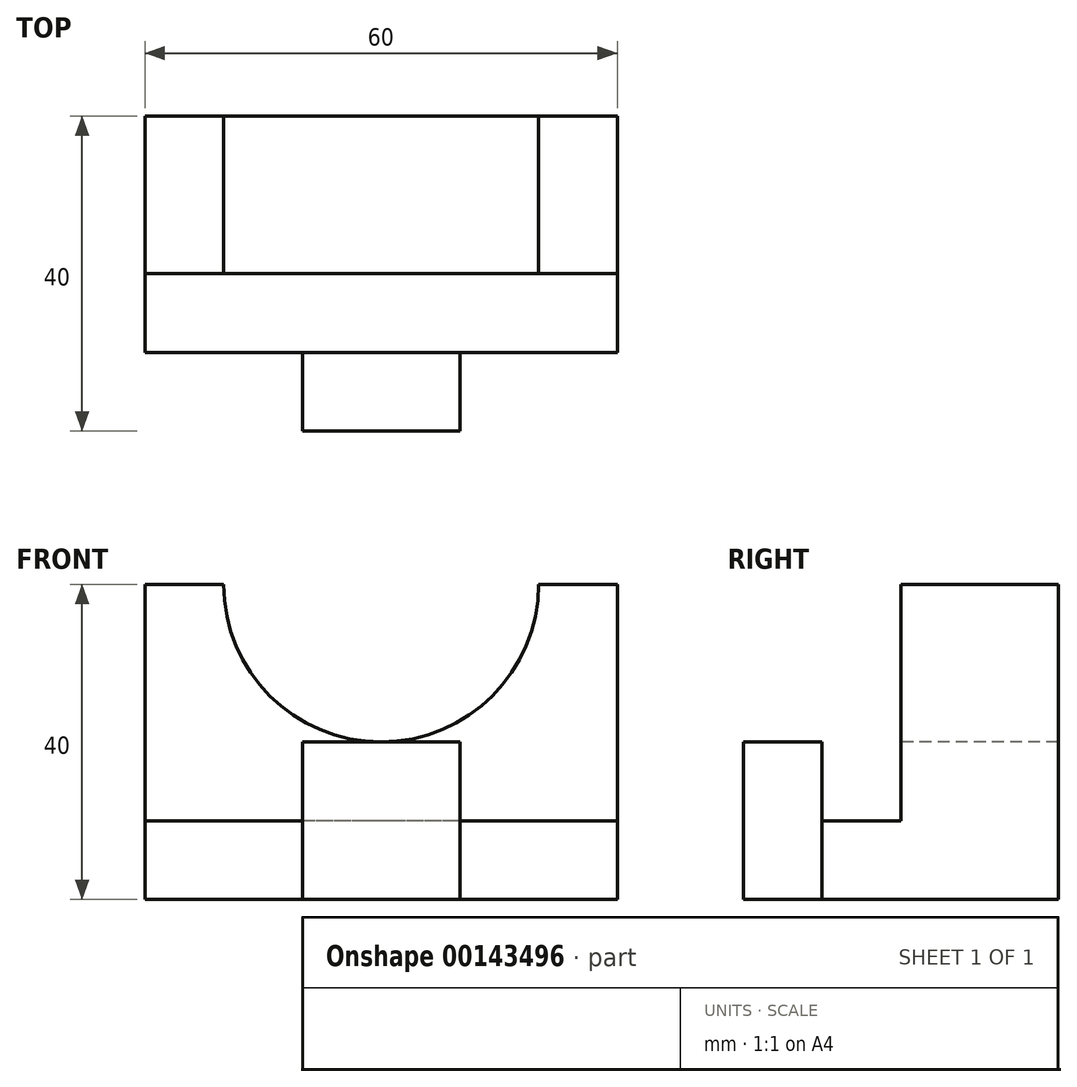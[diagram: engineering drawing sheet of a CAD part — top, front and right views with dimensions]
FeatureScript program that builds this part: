
annotation { "Feature Type Name" : "Feature", "Feature Type Description" : "" }
export const myFeature = defineFeature(function(context is Context, id is Id, definition is map)
    precondition{}
    {
        {
            var Q0;
            Q0=qCreatedBy(makeId("Right.planeOp"),FACE);
            var sketch = newSketch(context, id + "F0", { "sketchPlane" : qUnion([Q0])});
            skLineSegment(sketch, "E0", {"start": v(0, 0) * mm, "end": v(0, 40) * mm});
            skLineSegment(sketch, "E1", {"start": v(0, 40) * mm, "end": v(-20, 40) * mm});
            skLineSegment(sketch, "E2", {"start": v(-20, 40) * mm, "end": v(-20, 10) * mm});
            skLineSegment(sketch, "E3", {"start": v(-20, 10) * mm, "end": v(-30, 10) * mm});
            skLineSegment(sketch, "E4", {"start": v(-30, 10) * mm, "end": v(-30, 0) * mm});
            skLineSegment(sketch, "E5", {"start": v(-30, 0) * mm, "end": v(0, 0) * mm});
            skSolve(sketch);
        }
        {
            var Q0;
            Q0=makeQuery(id+"F0.imprint","IMPRINT",FACE,{"disambiguationData":[TD([[makeQuery(id+"F0.imprint","IMPRINT",EDGE,{"derivedFrom":sQuery(id+"F0.wireOp",EDGE,"E0")}),1.0]])]});
            extrude(context, id + "F1", {"entities" : qUnion([Q0]), "endBound" : BoundingType.SYMMETRIC, "depth" : 60 * mm});
        }
        {
            var Q0;
            Q0=makeQuery(id+"F1.opExtrude","SWEPT_FACE",FACE,{"disambiguationData":[OSD([sQuery(id+"F0.wireOp",EDGE,"E2")])]});
            var sketch = newSketch(context, id + "F2", { "sketchPlane" : qUnion([Q0])});
            skArc(sketch, "E6", {"start": v(-20, 40) * mm, "mid": v(0, 20) * mm, "end": v(20, 40) * mm});
            skLineSegment(sketch, "E7", {"start": v(-20, 40) * mm, "end": v(20, 40) * mm});
            skSolve(sketch);
        }
        {
            var Q0;
            Q0=makeQuery(id+"F2.imprint","IMPRINT",FACE,{"disambiguationData":[TD([[makeQuery(id+"F2.imprint","IMPRINT",EDGE,{"derivedFrom":sQuery(id+"F2.wireOp",EDGE,"E6")}),1.0]])]});
            extrude(context, id + "F3", {"entities" : qUnion([Q0]), "operationType" : NewBodyOperationType.REMOVE, "endBound" : BoundingType.THROUGH_ALL, "oppositeDirection" : true, "depth" : 25 * mm});
        }
        {
            var Q0;
            Q0=makeQuery(id+"F1.opExtrude","SWEPT_FACE",FACE,{"disambiguationData":[OSD([sQuery(id+"F0.wireOp",EDGE,"E4")])]});
            var sketch = newSketch(context, id + "F4", { "sketchPlane" : qUnion([Q0])});
            skLineSegment(sketch, "E8.bottom", {"start": v(-10, 0) * mm, "end": v(10, 0) * mm});
            skLineSegment(sketch, "E8.top", {"start": v(-10, 20) * mm, "end": v(10, 20) * mm});
            skLineSegment(sketch, "E8.left", {"start": v(-10, 0) * mm, "end": v(-10, 20) * mm});
            skLineSegment(sketch, "E8.right", {"start": v(10, 0) * mm, "end": v(10, 20) * mm});
            skLineSegment(sketch, "E9", {"start": v(0, 26.92) * mm, "end": v(0, -9.46) * mm, "construction": true});
            skSolve(sketch);
        }
        {
            var Q0;
            {var subQ0=sQuery(id+"F4.wireOp",EDGE,"E8.bottom");Q0=makeQuery(id+"F4.imprint","IMPRINT",FACE,{"disambiguationData":[TD([[makeQuery(id+"F4.imprint","IMPRINT",EDGE,{"derivedFrom":subQ0}),-1.0]])]});}
            var Q1;
            {var subQ0=sQuery(id+"F4.wireOp",EDGE,"E8.top");Q1=makeQuery(id+"F4.imprint","IMPRINT",FACE,{"disambiguationData":[TD([[makeQuery(id+"F4.imprint","IMPRINT",EDGE,{"derivedFrom":subQ0}),-1.0]])]});}
            extrude(context, id + "F5", {"entities" : qUnion([Q0, Q1]), "operationType" : NewBodyOperationType.ADD, "depth" : 10 * mm});
        }
    });
